# Revit family: CBP
name_source: partatom
category: Air Terminals
revit_build: Autodesk Revit MEP 2012 (Build: 20110309_2315(x64)
units: mm (PartAtom-declared; Revit-internal decimal feet)

## types (4) — shared parameters
Manufacturer = INNES
Máxima presión estática = 0.00 in-wg
Máxima velocidad de cuello = 0 FPM
Mínima presión estática = 0.00 in-wg
Mínima velocidad de cuello = 0 FPM
URL = http://www.innes.com.mx

## per-type parameters (varying)
| type | Altura H | Ancho W | Ancho espesor W | Centro circunferencia A | Centro circunferencia C | Largo L | Largo espesor L | Radio D | Radio ext D |
| CBP-06 | 11 1/8" | 12 7/8" | 12 5/8" | 7 1/8" | 6 9/16" | 12 3/8" | 12 1/8" | 2 15/16" | 3 1/16" |
| CBP-10 | 13 1/8" | 14 7/8" | 14 5/8" | 8 1/8" | 6 9/16" | 14 3/8" | 14 1/8" | 4 15/16" | 5 1/16" |
| CBP-12 | 17 1/8" | 18 7/8" | 18 5/8" | 10 1/8" | 8 9/16" | 18 3/8" | 18 1/8" | 5 15/16" | 6 1/16" |
| CBP-16 | 21 1/8" | 22 7/8" | 22 5/8" | 12 1/8" | 10 9/16" | 22 3/8" | 22 1/8" | 7 15/16" | 8 1/16" |

## geometry (parser evidence)
native form markers: Sweep x1
no freeform markers — native parametric forms only
